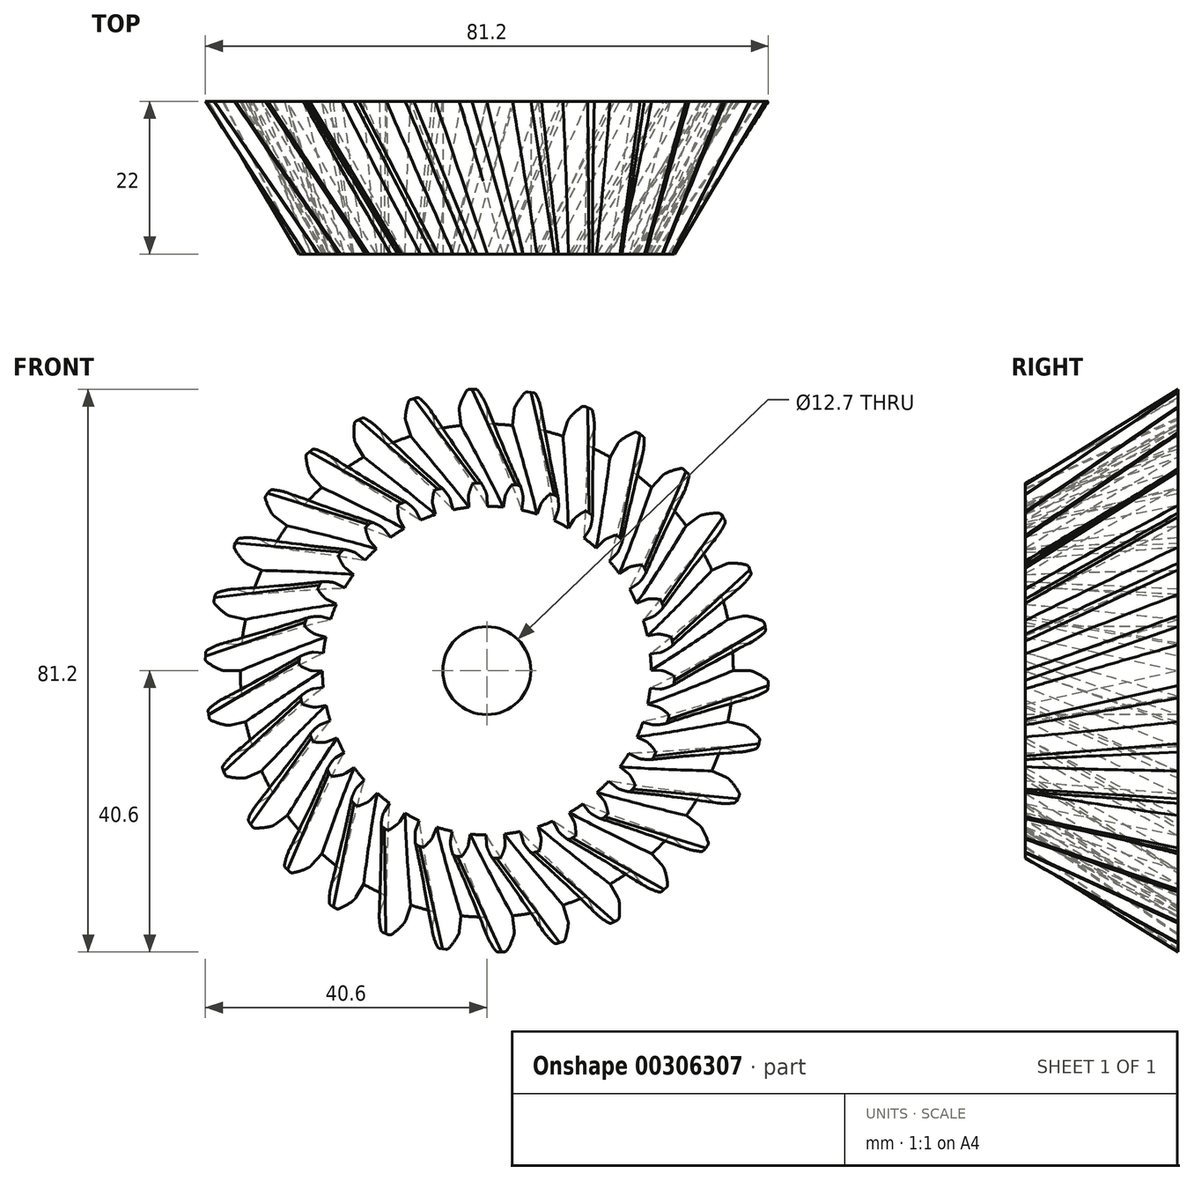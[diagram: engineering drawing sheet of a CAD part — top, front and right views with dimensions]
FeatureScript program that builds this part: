
annotation { "Feature Type Name" : "Feature", "Feature Type Description" : "" }
export const myFeature = defineFeature(function(context is Context, id is Id, definition is map)
    precondition{}
    {
        {
            var Q0;
            Q0=qCreatedBy(makeId("Front.planeOp"),FACE);
            var sketch = newSketch(context, id + "F0", { "sketchPlane" : qUnion([Q0])});
            skCircle(sketch, "E0", {"center": v(0, 0) * mm, "radius": 35.56 * mm});
            skArc(sketch, "E1", {"start": v(-0.13, 38.41) * mm, "mid": v(-0.64, 39.44) * mm, "end": v(-1.27, 40.4) * mm});
            skLineSegment(sketch, "E2", {"start": v(-1.7, 40.6) * mm, "end": v(-2.13, 40.58) * mm});
            skLineSegment(sketch, "E3", {"start": v(0, 37.8) * mm, "end": v(0, 35.56) * mm});
            skLineSegment(sketch, "E4.MirrorCS", {"start": v(-2.55, 40.56) * mm, "end": v(-2.13, 40.58) * mm});
            skArc(sketch, "E5.MirrorCS", {"start": v(-3.89, 38.22) * mm, "mid": v(-3.49, 39.3) * mm, "end": v(-2.96, 40.3) * mm});
            skLineSegment(sketch, "E6.MirrorCS", {"start": v(-3.95, 37.58) * mm, "end": v(-3.72, 35.37) * mm});
            skPoint(sketch, "E7.visualSharp", {"position": v(-1.44, 40.61) * mm});
            skArc(sketch, "E7.filletArc", {"start": v(-1.27, 40.4) * mm, "mid": v(-1.46, 40.55) * mm, "end": v(-1.7, 40.6) * mm});
            skPoint(sketch, "E8.visualSharp", {"position": v(-2.81, 40.54) * mm});
            skArc(sketch, "E8.filletArc", {"start": v(-2.55, 40.56) * mm, "mid": v(-2.78, 40.48) * mm, "end": v(-2.96, 40.3) * mm});
            skPoint(sketch, "E9.visualSharp", {"position": v(0, 38.1) * mm});
            skArc(sketch, "E9.filletArc", {"start": v(0, 37.8) * mm, "mid": v(-0.03, 38.1) * mm, "end": v(-0.13, 38.41) * mm});
            skPoint(sketch, "E10.visualSharp", {"position": v(-3.98, 37.9) * mm});
            skArc(sketch, "E10.filletArc", {"start": v(-3.89, 38.22) * mm, "mid": v(-3.95, 37.9) * mm, "end": v(-3.95, 37.58) * mm});
            skLineSegment(sketch, "E11.1.0", {"start": v(-11.68, 35.94) * mm, "end": v(-10.99, 33.82) * mm});
            skArc(sketch, "E11.1.1", {"start": v(-11.75, 36.57) * mm, "mid": v(-11.75, 36.25) * mm, "end": v(-11.68, 35.94) * mm});
            skArc(sketch, "E11.1.2", {"start": v(-11.75, 36.57) * mm, "mid": v(-11.58, 37.7) * mm, "end": v(-11.27, 38.81) * mm});
            skArc(sketch, "E11.1.3", {"start": v(-10.92, 39.14) * mm, "mid": v(-11.14, 39.02) * mm, "end": v(-11.27, 38.81) * mm});
            skLineSegment(sketch, "E11.1.4", {"start": v(-10.92, 39.14) * mm, "end": v(-10.52, 39.25) * mm});
            skLineSegment(sketch, "E11.1.5", {"start": v(-10.1, 39.36) * mm, "end": v(-10.52, 39.25) * mm});
            skArc(sketch, "E11.1.6", {"start": v(-9.64, 39.25) * mm, "mid": v(-9.86, 39.36) * mm, "end": v(-10.1, 39.36) * mm});
            skArc(sketch, "E11.1.7", {"start": v(-8.11, 37.55) * mm, "mid": v(-8.83, 38.45) * mm, "end": v(-9.64, 39.25) * mm});
            skArc(sketch, "E11.1.8", {"start": v(-7.86, 36.97) * mm, "mid": v(-7.95, 37.27) * mm, "end": v(-8.11, 37.55) * mm});
            skLineSegment(sketch, "E11.1.9", {"start": v(-7.86, 36.97) * mm, "end": v(-7.4, 34.78) * mm});
            skLineSegment(sketch, "E11.2.0", {"start": v(-18.9, 32.73) * mm, "end": v(-17.78, 30.8) * mm});
            skArc(sketch, "E11.2.1", {"start": v(-19.1, 33.33) * mm, "mid": v(-19.03, 33.02) * mm, "end": v(-18.9, 32.73) * mm});
            skArc(sketch, "E11.2.2", {"start": v(-19.1, 33.33) * mm, "mid": v(-19.17, 34.48) * mm, "end": v(-19.1, 35.62) * mm});
            skArc(sketch, "E11.2.3", {"start": v(-18.82, 36.01) * mm, "mid": v(-19, 35.85) * mm, "end": v(-19.1, 35.62) * mm});
            skLineSegment(sketch, "E11.2.4", {"start": v(-18.82, 36.01) * mm, "end": v(-18.45, 36.2) * mm});
            skLineSegment(sketch, "E11.2.5", {"start": v(-18.07, 36.4) * mm, "end": v(-18.45, 36.2) * mm});
            skArc(sketch, "E11.2.6", {"start": v(-17.6, 36.39) * mm, "mid": v(-17.83, 36.45) * mm, "end": v(-18.07, 36.4) * mm});
            skArc(sketch, "E11.2.7", {"start": v(-15.74, 35.04) * mm, "mid": v(-16.63, 35.77) * mm, "end": v(-17.6, 36.39) * mm});
            skArc(sketch, "E11.2.8", {"start": v(-15.37, 34.52) * mm, "mid": v(-15.53, 34.8) * mm, "end": v(-15.74, 35.04) * mm});
            skLineSegment(sketch, "E11.2.9", {"start": v(-15.37, 34.52) * mm, "end": v(-14.46, 32.49) * mm});
            skLineSegment(sketch, "E11.3.0", {"start": v(-25.29, 28.08) * mm, "end": v(-23.8, 26.43) * mm});
            skArc(sketch, "E11.3.1", {"start": v(-25.6, 28.63) * mm, "mid": v(-25.48, 28.34) * mm, "end": v(-25.29, 28.08) * mm});
            skArc(sketch, "E11.3.2", {"start": v(-25.6, 28.63) * mm, "mid": v(-25.92, 29.74) * mm, "end": v(-26.09, 30.87) * mm});
            skArc(sketch, "E11.3.3", {"start": v(-25.9, 31.31) * mm, "mid": v(-26.05, 31.12) * mm, "end": v(-26.09, 30.87) * mm});
            skLineSegment(sketch, "E11.3.4", {"start": v(-25.9, 31.31) * mm, "end": v(-25.57, 31.58) * mm});
            skLineSegment(sketch, "E11.3.5", {"start": v(-25.24, 31.84) * mm, "end": v(-25.57, 31.58) * mm});
            skArc(sketch, "E11.3.6", {"start": v(-24.77, 31.94) * mm, "mid": v(-25.02, 31.95) * mm, "end": v(-25.24, 31.84) * mm});
            skArc(sketch, "E11.3.7", {"start": v(-22.68, 31) * mm, "mid": v(-23.7, 31.53) * mm, "end": v(-24.77, 31.94) * mm});
            skArc(sketch, "E11.3.8", {"start": v(-22.21, 30.57) * mm, "mid": v(-22.43, 30.81) * mm, "end": v(-22.68, 31) * mm});
            skLineSegment(sketch, "E11.3.9", {"start": v(-22.21, 30.57) * mm, "end": v(-20.9, 28.77) * mm});
            skLineSegment(sketch, "E11.4.0", {"start": v(-30.57, 22.21) * mm, "end": v(-28.77, 20.9) * mm});
            skArc(sketch, "E11.4.1", {"start": v(-31, 22.68) * mm, "mid": v(-30.81, 22.43) * mm, "end": v(-30.57, 22.21) * mm});
            skArc(sketch, "E11.4.2", {"start": v(-31, 22.68) * mm, "mid": v(-31.53, 23.7) * mm, "end": v(-31.94, 24.77) * mm});
            skArc(sketch, "E11.4.3", {"start": v(-31.84, 25.24) * mm, "mid": v(-31.95, 25.02) * mm, "end": v(-31.94, 24.77) * mm});
            skLineSegment(sketch, "E11.4.4", {"start": v(-31.84, 25.24) * mm, "end": v(-31.58, 25.57) * mm});
            skLineSegment(sketch, "E11.4.5", {"start": v(-31.31, 25.9) * mm, "end": v(-31.58, 25.57) * mm});
            skArc(sketch, "E11.4.6", {"start": v(-30.87, 26.09) * mm, "mid": v(-31.12, 26.05) * mm, "end": v(-31.31, 25.9) * mm});
            skArc(sketch, "E11.4.7", {"start": v(-28.63, 25.6) * mm, "mid": v(-29.74, 25.92) * mm, "end": v(-30.87, 26.09) * mm});
            skArc(sketch, "E11.4.8", {"start": v(-28.08, 25.29) * mm, "mid": v(-28.34, 25.48) * mm, "end": v(-28.63, 25.6) * mm});
            skLineSegment(sketch, "E11.4.9", {"start": v(-28.08, 25.29) * mm, "end": v(-26.43, 23.8) * mm});
            skLineSegment(sketch, "E11.5.0", {"start": v(-34.52, 15.37) * mm, "end": v(-32.49, 14.46) * mm});
            skArc(sketch, "E11.5.1", {"start": v(-35.04, 15.74) * mm, "mid": v(-34.8, 15.53) * mm, "end": v(-34.52, 15.37) * mm});
            skArc(sketch, "E11.5.2", {"start": v(-35.04, 15.74) * mm, "mid": v(-35.77, 16.63) * mm, "end": v(-36.39, 17.6) * mm});
            skArc(sketch, "E11.5.3", {"start": v(-36.4, 18.07) * mm, "mid": v(-36.45, 17.83) * mm, "end": v(-36.39, 17.6) * mm});
            skLineSegment(sketch, "E11.5.4", {"start": v(-36.4, 18.07) * mm, "end": v(-36.2, 18.45) * mm});
            skLineSegment(sketch, "E11.5.5", {"start": v(-36.01, 18.82) * mm, "end": v(-36.2, 18.45) * mm});
            skArc(sketch, "E11.5.6", {"start": v(-35.62, 19.1) * mm, "mid": v(-35.85, 19) * mm, "end": v(-36.01, 18.82) * mm});
            skArc(sketch, "E11.5.7", {"start": v(-33.33, 19.1) * mm, "mid": v(-34.48, 19.17) * mm, "end": v(-35.62, 19.1) * mm});
            skArc(sketch, "E11.5.8", {"start": v(-32.73, 18.9) * mm, "mid": v(-33.02, 19.03) * mm, "end": v(-33.33, 19.1) * mm});
            skLineSegment(sketch, "E11.5.9", {"start": v(-32.73, 18.9) * mm, "end": v(-30.8, 17.78) * mm});
            skLineSegment(sketch, "E11.6.0", {"start": v(-36.97, 7.86) * mm, "end": v(-34.78, 7.4) * mm});
            skArc(sketch, "E11.6.1", {"start": v(-37.55, 8.11) * mm, "mid": v(-37.27, 7.95) * mm, "end": v(-36.97, 7.86) * mm});
            skArc(sketch, "E11.6.2", {"start": v(-37.55, 8.11) * mm, "mid": v(-38.45, 8.83) * mm, "end": v(-39.25, 9.64) * mm});
            skArc(sketch, "E11.6.3", {"start": v(-39.36, 10.1) * mm, "mid": v(-39.36, 9.86) * mm, "end": v(-39.25, 9.64) * mm});
            skLineSegment(sketch, "E11.6.4", {"start": v(-39.36, 10.1) * mm, "end": v(-39.25, 10.52) * mm});
            skLineSegment(sketch, "E11.6.5", {"start": v(-39.14, 10.92) * mm, "end": v(-39.25, 10.52) * mm});
            skArc(sketch, "E11.6.6", {"start": v(-38.81, 11.27) * mm, "mid": v(-39.02, 11.14) * mm, "end": v(-39.14, 10.92) * mm});
            skArc(sketch, "E11.6.7", {"start": v(-36.57, 11.75) * mm, "mid": v(-37.7, 11.58) * mm, "end": v(-38.81, 11.27) * mm});
            skArc(sketch, "E11.6.8", {"start": v(-35.94, 11.68) * mm, "mid": v(-36.25, 11.75) * mm, "end": v(-36.57, 11.75) * mm});
            skLineSegment(sketch, "E11.6.9", {"start": v(-35.94, 11.68) * mm, "end": v(-33.82, 10.99) * mm});
            skLineSegment(sketch, "E11.7.0", {"start": v(-37.8, 0) * mm, "end": v(-35.56, 0) * mm});
            skArc(sketch, "E11.7.1", {"start": v(-38.41, 0.13) * mm, "mid": v(-38.1, 0.03) * mm, "end": v(-37.8, 0) * mm});
            skArc(sketch, "E11.7.2", {"start": v(-38.41, 0.13) * mm, "mid": v(-39.44, 0.64) * mm, "end": v(-40.4, 1.27) * mm});
            skArc(sketch, "E11.7.3", {"start": v(-40.6, 1.7) * mm, "mid": v(-40.55, 1.46) * mm, "end": v(-40.4, 1.27) * mm});
            skLineSegment(sketch, "E11.7.4", {"start": v(-40.6, 1.7) * mm, "end": v(-40.58, 2.13) * mm});
            skLineSegment(sketch, "E11.7.5", {"start": v(-40.56, 2.55) * mm, "end": v(-40.58, 2.13) * mm});
            skArc(sketch, "E11.7.6", {"start": v(-40.3, 2.96) * mm, "mid": v(-40.48, 2.78) * mm, "end": v(-40.56, 2.55) * mm});
            skArc(sketch, "E11.7.7", {"start": v(-38.22, 3.89) * mm, "mid": v(-39.3, 3.49) * mm, "end": v(-40.3, 2.96) * mm});
            skArc(sketch, "E11.7.8", {"start": v(-37.58, 3.95) * mm, "mid": v(-37.9, 3.95) * mm, "end": v(-38.22, 3.89) * mm});
            skLineSegment(sketch, "E11.7.9", {"start": v(-37.58, 3.95) * mm, "end": v(-35.37, 3.72) * mm});
            skLineSegment(sketch, "E11.8.0", {"start": v(-36.97, -7.86) * mm, "end": v(-34.78, -7.4) * mm});
            skArc(sketch, "E11.8.1", {"start": v(-37.6, -7.86) * mm, "mid": v(-37.28, -7.9) * mm, "end": v(-36.97, -7.86) * mm});
            skArc(sketch, "E11.8.2", {"start": v(-37.6, -7.86) * mm, "mid": v(-38.71, -7.57) * mm, "end": v(-39.78, -7.16) * mm});
            skArc(sketch, "E11.8.3", {"start": v(-40.07, -6.77) * mm, "mid": v(-39.97, -7) * mm, "end": v(-39.78, -7.16) * mm});
            skLineSegment(sketch, "E11.8.4", {"start": v(-40.07, -6.77) * mm, "end": v(-40.13, -6.36) * mm});
            skLineSegment(sketch, "E11.8.5", {"start": v(-40.2, -5.94) * mm, "end": v(-40.13, -6.36) * mm});
            skArc(sketch, "E11.8.6", {"start": v(-40.04, -5.49) * mm, "mid": v(-40.18, -5.7) * mm, "end": v(-40.2, -5.94) * mm});
            skArc(sketch, "E11.8.7", {"start": v(-38.19, -4.14) * mm, "mid": v(-39.16, -4.76) * mm, "end": v(-40.04, -5.49) * mm});
            skArc(sketch, "E11.8.8", {"start": v(-37.58, -3.95) * mm, "mid": v(-37.9, -4.02) * mm, "end": v(-38.19, -4.14) * mm});
            skLineSegment(sketch, "E11.8.9", {"start": v(-37.58, -3.95) * mm, "end": v(-35.37, -3.72) * mm});
            skLineSegment(sketch, "E11.9.0", {"start": v(-34.52, -15.37) * mm, "end": v(-32.49, -14.46) * mm});
            skArc(sketch, "E11.9.1", {"start": v(-35.14, -15.5) * mm, "mid": v(-34.83, -15.47) * mm, "end": v(-34.52, -15.37) * mm});
            skArc(sketch, "E11.9.2", {"start": v(-35.14, -15.5) * mm, "mid": v(-36.3, -15.46) * mm, "end": v(-37.42, -15.27) * mm});
            skArc(sketch, "E11.9.3", {"start": v(-37.78, -14.96) * mm, "mid": v(-37.64, -15.16) * mm, "end": v(-37.42, -15.27) * mm});
            skLineSegment(sketch, "E11.9.4", {"start": v(-37.78, -14.96) * mm, "end": v(-37.94, -14.56) * mm});
            skLineSegment(sketch, "E11.9.5", {"start": v(-38.09, -14.17) * mm, "end": v(-37.94, -14.56) * mm});
            skArc(sketch, "E11.9.6", {"start": v(-38.03, -13.7) * mm, "mid": v(-38.12, -13.92) * mm, "end": v(-38.09, -14.17) * mm});
            skArc(sketch, "E11.9.7", {"start": v(-36.5, -12) * mm, "mid": v(-37.31, -12.8) * mm, "end": v(-38.03, -13.7) * mm});
            skArc(sketch, "E11.9.8", {"start": v(-35.94, -11.68) * mm, "mid": v(-36.23, -11.8) * mm, "end": v(-36.5, -12) * mm});
            skLineSegment(sketch, "E11.9.9", {"start": v(-35.94, -11.68) * mm, "end": v(-33.82, -10.99) * mm});
            skLineSegment(sketch, "E11.10.0", {"start": v(-30.57, -22.21) * mm, "end": v(-28.77, -20.9) * mm});
            skArc(sketch, "E11.10.1", {"start": v(-31.15, -22.48) * mm, "mid": v(-30.85, -22.37) * mm, "end": v(-30.57, -22.21) * mm});
            skArc(sketch, "E11.10.2", {"start": v(-31.15, -22.48) * mm, "mid": v(-32.28, -22.67) * mm, "end": v(-33.43, -22.72) * mm});
            skArc(sketch, "E11.10.3", {"start": v(-33.85, -22.49) * mm, "mid": v(-33.67, -22.65) * mm, "end": v(-33.43, -22.72) * mm});
            skLineSegment(sketch, "E11.10.4", {"start": v(-33.85, -22.49) * mm, "end": v(-34.08, -22.13) * mm});
            skLineSegment(sketch, "E11.10.5", {"start": v(-34.3, -21.78) * mm, "end": v(-34.08, -22.13) * mm});
            skArc(sketch, "E11.10.6", {"start": v(-34.35, -21.3) * mm, "mid": v(-34.39, -21.54) * mm, "end": v(-34.3, -21.78) * mm});
            skArc(sketch, "E11.10.7", {"start": v(-33.2, -19.32) * mm, "mid": v(-33.84, -20.27) * mm, "end": v(-34.35, -21.3) * mm});
            skArc(sketch, "E11.10.8", {"start": v(-32.73, -18.9) * mm, "mid": v(-32.99, -19.08) * mm, "end": v(-33.2, -19.32) * mm});
            skLineSegment(sketch, "E11.10.9", {"start": v(-32.73, -18.9) * mm, "end": v(-30.8, -17.78) * mm});
            skLineSegment(sketch, "E11.11.0", {"start": v(-25.29, -28.08) * mm, "end": v(-23.8, -26.43) * mm});
            skArc(sketch, "E11.11.1", {"start": v(-25.8, -28.46) * mm, "mid": v(-25.52, -28.3) * mm, "end": v(-25.29, -28.08) * mm});
            skArc(sketch, "E11.11.2", {"start": v(-25.8, -28.46) * mm, "mid": v(-26.87, -28.88) * mm, "end": v(-27.98, -29.17) * mm});
            skArc(sketch, "E11.11.3", {"start": v(-28.43, -29.03) * mm, "mid": v(-28.22, -29.16) * mm, "end": v(-27.98, -29.17) * mm});
            skLineSegment(sketch, "E11.11.4", {"start": v(-28.43, -29.03) * mm, "end": v(-28.73, -28.73) * mm});
            skLineSegment(sketch, "E11.11.5", {"start": v(-29.03, -28.43) * mm, "end": v(-28.73, -28.73) * mm});
            skArc(sketch, "E11.11.6", {"start": v(-29.17, -27.98) * mm, "mid": v(-29.16, -28.22) * mm, "end": v(-29.03, -28.43) * mm});
            skArc(sketch, "E11.11.7", {"start": v(-28.46, -25.8) * mm, "mid": v(-28.88, -26.87) * mm, "end": v(-29.17, -27.98) * mm});
            skArc(sketch, "E11.11.8", {"start": v(-28.08, -25.29) * mm, "mid": v(-28.3, -25.52) * mm, "end": v(-28.46, -25.8) * mm});
            skLineSegment(sketch, "E11.11.9", {"start": v(-28.08, -25.29) * mm, "end": v(-26.43, -23.8) * mm});
            skLineSegment(sketch, "E11.12.0", {"start": v(-18.9, -32.73) * mm, "end": v(-17.78, -30.8) * mm});
            skArc(sketch, "E11.12.1", {"start": v(-19.32, -33.2) * mm, "mid": v(-19.08, -32.99) * mm, "end": v(-18.9, -32.73) * mm});
            skArc(sketch, "E11.12.2", {"start": v(-19.32, -33.2) * mm, "mid": v(-20.27, -33.84) * mm, "end": v(-21.3, -34.35) * mm});
            skArc(sketch, "E11.12.3", {"start": v(-21.78, -34.3) * mm, "mid": v(-21.54, -34.39) * mm, "end": v(-21.3, -34.35) * mm});
            skLineSegment(sketch, "E11.12.4", {"start": v(-21.78, -34.3) * mm, "end": v(-22.13, -34.08) * mm});
            skLineSegment(sketch, "E11.12.5", {"start": v(-22.49, -33.85) * mm, "end": v(-22.13, -34.08) * mm});
            skArc(sketch, "E11.12.6", {"start": v(-22.72, -33.43) * mm, "mid": v(-22.65, -33.67) * mm, "end": v(-22.49, -33.85) * mm});
            skArc(sketch, "E11.12.7", {"start": v(-22.48, -31.15) * mm, "mid": v(-22.67, -32.28) * mm, "end": v(-22.72, -33.43) * mm});
            skArc(sketch, "E11.12.8", {"start": v(-22.21, -30.57) * mm, "mid": v(-22.37, -30.85) * mm, "end": v(-22.48, -31.15) * mm});
            skLineSegment(sketch, "E11.12.9", {"start": v(-22.21, -30.57) * mm, "end": v(-20.9, -28.77) * mm});
            skLineSegment(sketch, "E11.13.0", {"start": v(-11.68, -35.94) * mm, "end": v(-10.99, -33.82) * mm});
            skArc(sketch, "E11.13.1", {"start": v(-12, -36.5) * mm, "mid": v(-11.8, -36.23) * mm, "end": v(-11.68, -35.94) * mm});
            skArc(sketch, "E11.13.2", {"start": v(-12, -36.5) * mm, "mid": v(-12.8, -37.31) * mm, "end": v(-13.7, -38.03) * mm});
            skArc(sketch, "E11.13.3", {"start": v(-14.17, -38.09) * mm, "mid": v(-13.92, -38.12) * mm, "end": v(-13.7, -38.03) * mm});
            skLineSegment(sketch, "E11.13.4", {"start": v(-14.17, -38.09) * mm, "end": v(-14.56, -37.94) * mm});
            skLineSegment(sketch, "E11.13.5", {"start": v(-14.96, -37.78) * mm, "end": v(-14.56, -37.94) * mm});
            skArc(sketch, "E11.13.6", {"start": v(-15.27, -37.42) * mm, "mid": v(-15.16, -37.64) * mm, "end": v(-14.96, -37.78) * mm});
            skArc(sketch, "E11.13.7", {"start": v(-15.5, -35.14) * mm, "mid": v(-15.46, -36.3) * mm, "end": v(-15.27, -37.42) * mm});
            skArc(sketch, "E11.13.8", {"start": v(-15.37, -34.52) * mm, "mid": v(-15.47, -34.83) * mm, "end": v(-15.5, -35.14) * mm});
            skLineSegment(sketch, "E11.13.9", {"start": v(-15.37, -34.52) * mm, "end": v(-14.46, -32.49) * mm});
            skLineSegment(sketch, "E11.14.0", {"start": v(-3.95, -37.58) * mm, "end": v(-3.72, -35.37) * mm});
            skArc(sketch, "E11.14.1", {"start": v(-4.14, -38.19) * mm, "mid": v(-4.02, -37.9) * mm, "end": v(-3.95, -37.58) * mm});
            skArc(sketch, "E11.14.2", {"start": v(-4.14, -38.19) * mm, "mid": v(-4.76, -39.16) * mm, "end": v(-5.49, -40.04) * mm});
            skArc(sketch, "E11.14.3", {"start": v(-5.94, -40.2) * mm, "mid": v(-5.7, -40.18) * mm, "end": v(-5.49, -40.04) * mm});
            skLineSegment(sketch, "E11.14.4", {"start": v(-5.94, -40.2) * mm, "end": v(-6.36, -40.13) * mm});
            skLineSegment(sketch, "E11.14.5", {"start": v(-6.77, -40.07) * mm, "end": v(-6.36, -40.13) * mm});
            skArc(sketch, "E11.14.6", {"start": v(-7.16, -39.78) * mm, "mid": v(-7, -39.97) * mm, "end": v(-6.77, -40.07) * mm});
            skArc(sketch, "E11.14.7", {"start": v(-7.86, -37.6) * mm, "mid": v(-7.57, -38.71) * mm, "end": v(-7.16, -39.78) * mm});
            skArc(sketch, "E11.14.8", {"start": v(-7.86, -36.97) * mm, "mid": v(-7.9, -37.28) * mm, "end": v(-7.86, -37.6) * mm});
            skLineSegment(sketch, "E11.14.9", {"start": v(-7.86, -36.97) * mm, "end": v(-7.4, -34.78) * mm});
            skLineSegment(sketch, "E11.15.0", {"start": v(3.95, -37.58) * mm, "end": v(3.72, -35.37) * mm});
            skArc(sketch, "E11.15.1", {"start": v(3.89, -38.22) * mm, "mid": v(3.95, -37.9) * mm, "end": v(3.95, -37.58) * mm});
            skArc(sketch, "E11.15.2", {"start": v(3.89, -38.22) * mm, "mid": v(3.49, -39.3) * mm, "end": v(2.96, -40.3) * mm});
            skArc(sketch, "E11.15.3", {"start": v(2.55, -40.56) * mm, "mid": v(2.78, -40.48) * mm, "end": v(2.96, -40.3) * mm});
            skLineSegment(sketch, "E11.15.4", {"start": v(2.55, -40.56) * mm, "end": v(2.13, -40.58) * mm});
            skLineSegment(sketch, "E11.15.5", {"start": v(1.7, -40.6) * mm, "end": v(2.13, -40.58) * mm});
            skArc(sketch, "E11.15.6", {"start": v(1.27, -40.4) * mm, "mid": v(1.46, -40.55) * mm, "end": v(1.7, -40.6) * mm});
            skArc(sketch, "E11.15.7", {"start": v(0.13, -38.41) * mm, "mid": v(0.64, -39.44) * mm, "end": v(1.27, -40.4) * mm});
            skArc(sketch, "E11.15.8", {"start": v(0, -37.8) * mm, "mid": v(0.03, -38.1) * mm, "end": v(0.13, -38.41) * mm});
            skLineSegment(sketch, "E11.15.9", {"start": v(0, -37.8) * mm, "end": v(0, -35.56) * mm});
            skLineSegment(sketch, "E11.16.0", {"start": v(11.68, -35.94) * mm, "end": v(10.99, -33.82) * mm});
            skArc(sketch, "E11.16.1", {"start": v(11.75, -36.57) * mm, "mid": v(11.75, -36.25) * mm, "end": v(11.68, -35.94) * mm});
            skArc(sketch, "E11.16.2", {"start": v(11.75, -36.57) * mm, "mid": v(11.58, -37.7) * mm, "end": v(11.27, -38.81) * mm});
            skArc(sketch, "E11.16.3", {"start": v(10.92, -39.14) * mm, "mid": v(11.14, -39.02) * mm, "end": v(11.27, -38.81) * mm});
            skLineSegment(sketch, "E11.16.4", {"start": v(10.92, -39.14) * mm, "end": v(10.52, -39.25) * mm});
            skLineSegment(sketch, "E11.16.5", {"start": v(10.1, -39.36) * mm, "end": v(10.52, -39.25) * mm});
            skArc(sketch, "E11.16.6", {"start": v(9.64, -39.25) * mm, "mid": v(9.86, -39.36) * mm, "end": v(10.1, -39.36) * mm});
            skArc(sketch, "E11.16.7", {"start": v(8.11, -37.55) * mm, "mid": v(8.83, -38.45) * mm, "end": v(9.64, -39.25) * mm});
            skArc(sketch, "E11.16.8", {"start": v(7.86, -36.97) * mm, "mid": v(7.95, -37.27) * mm, "end": v(8.11, -37.55) * mm});
            skLineSegment(sketch, "E11.16.9", {"start": v(7.86, -36.97) * mm, "end": v(7.4, -34.78) * mm});
            skLineSegment(sketch, "E11.17.0", {"start": v(18.9, -32.73) * mm, "end": v(17.78, -30.8) * mm});
            skArc(sketch, "E11.17.1", {"start": v(19.1, -33.33) * mm, "mid": v(19.03, -33.02) * mm, "end": v(18.9, -32.73) * mm});
            skArc(sketch, "E11.17.2", {"start": v(19.1, -33.33) * mm, "mid": v(19.17, -34.48) * mm, "end": v(19.1, -35.62) * mm});
            skArc(sketch, "E11.17.3", {"start": v(18.82, -36.01) * mm, "mid": v(19, -35.85) * mm, "end": v(19.1, -35.62) * mm});
            skLineSegment(sketch, "E11.17.4", {"start": v(18.82, -36.01) * mm, "end": v(18.45, -36.2) * mm});
            skLineSegment(sketch, "E11.17.5", {"start": v(18.07, -36.4) * mm, "end": v(18.45, -36.2) * mm});
            skArc(sketch, "E11.17.6", {"start": v(17.6, -36.39) * mm, "mid": v(17.83, -36.45) * mm, "end": v(18.07, -36.4) * mm});
            skArc(sketch, "E11.17.7", {"start": v(15.74, -35.04) * mm, "mid": v(16.63, -35.77) * mm, "end": v(17.6, -36.39) * mm});
            skArc(sketch, "E11.17.8", {"start": v(15.37, -34.52) * mm, "mid": v(15.53, -34.8) * mm, "end": v(15.74, -35.04) * mm});
            skLineSegment(sketch, "E11.17.9", {"start": v(15.37, -34.52) * mm, "end": v(14.46, -32.49) * mm});
            skLineSegment(sketch, "E11.18.0", {"start": v(25.29, -28.08) * mm, "end": v(23.8, -26.43) * mm});
            skArc(sketch, "E11.18.1", {"start": v(25.6, -28.63) * mm, "mid": v(25.48, -28.34) * mm, "end": v(25.29, -28.08) * mm});
            skArc(sketch, "E11.18.2", {"start": v(25.6, -28.63) * mm, "mid": v(25.92, -29.74) * mm, "end": v(26.09, -30.87) * mm});
            skArc(sketch, "E11.18.3", {"start": v(25.9, -31.31) * mm, "mid": v(26.05, -31.12) * mm, "end": v(26.09, -30.87) * mm});
            skLineSegment(sketch, "E11.18.4", {"start": v(25.9, -31.31) * mm, "end": v(25.57, -31.58) * mm});
            skLineSegment(sketch, "E11.18.5", {"start": v(25.24, -31.84) * mm, "end": v(25.57, -31.58) * mm});
            skArc(sketch, "E11.18.6", {"start": v(24.77, -31.94) * mm, "mid": v(25.02, -31.95) * mm, "end": v(25.24, -31.84) * mm});
            skArc(sketch, "E11.18.7", {"start": v(22.68, -31) * mm, "mid": v(23.7, -31.53) * mm, "end": v(24.77, -31.94) * mm});
            skArc(sketch, "E11.18.8", {"start": v(22.21, -30.57) * mm, "mid": v(22.43, -30.81) * mm, "end": v(22.68, -31) * mm});
            skLineSegment(sketch, "E11.18.9", {"start": v(22.21, -30.57) * mm, "end": v(20.9, -28.77) * mm});
            skLineSegment(sketch, "E11.19.0", {"start": v(30.57, -22.21) * mm, "end": v(28.77, -20.9) * mm});
            skArc(sketch, "E11.19.1", {"start": v(31, -22.68) * mm, "mid": v(30.81, -22.43) * mm, "end": v(30.57, -22.21) * mm});
            skArc(sketch, "E11.19.2", {"start": v(31, -22.68) * mm, "mid": v(31.53, -23.7) * mm, "end": v(31.94, -24.77) * mm});
            skArc(sketch, "E11.19.3", {"start": v(31.84, -25.24) * mm, "mid": v(31.95, -25.02) * mm, "end": v(31.94, -24.77) * mm});
            skLineSegment(sketch, "E11.19.4", {"start": v(31.84, -25.24) * mm, "end": v(31.58, -25.57) * mm});
            skLineSegment(sketch, "E11.19.5", {"start": v(31.31, -25.9) * mm, "end": v(31.58, -25.57) * mm});
            skArc(sketch, "E11.19.6", {"start": v(30.87, -26.09) * mm, "mid": v(31.12, -26.05) * mm, "end": v(31.31, -25.9) * mm});
            skArc(sketch, "E11.19.7", {"start": v(28.63, -25.6) * mm, "mid": v(29.74, -25.92) * mm, "end": v(30.87, -26.09) * mm});
            skArc(sketch, "E11.19.8", {"start": v(28.08, -25.29) * mm, "mid": v(28.34, -25.48) * mm, "end": v(28.63, -25.6) * mm});
            skLineSegment(sketch, "E11.19.9", {"start": v(28.08, -25.29) * mm, "end": v(26.43, -23.8) * mm});
            skLineSegment(sketch, "E11.20.0", {"start": v(34.52, -15.37) * mm, "end": v(32.49, -14.46) * mm});
            skArc(sketch, "E11.20.1", {"start": v(35.04, -15.74) * mm, "mid": v(34.8, -15.53) * mm, "end": v(34.52, -15.37) * mm});
            skArc(sketch, "E11.20.2", {"start": v(35.04, -15.74) * mm, "mid": v(35.77, -16.63) * mm, "end": v(36.39, -17.6) * mm});
            skArc(sketch, "E11.20.3", {"start": v(36.4, -18.07) * mm, "mid": v(36.45, -17.83) * mm, "end": v(36.39, -17.6) * mm});
            skLineSegment(sketch, "E11.20.4", {"start": v(36.4, -18.07) * mm, "end": v(36.2, -18.45) * mm});
            skLineSegment(sketch, "E11.20.5", {"start": v(36.01, -18.82) * mm, "end": v(36.2, -18.45) * mm});
            skArc(sketch, "E11.20.6", {"start": v(35.62, -19.1) * mm, "mid": v(35.85, -19) * mm, "end": v(36.01, -18.82) * mm});
            skArc(sketch, "E11.20.7", {"start": v(33.33, -19.1) * mm, "mid": v(34.48, -19.17) * mm, "end": v(35.62, -19.1) * mm});
            skArc(sketch, "E11.20.8", {"start": v(32.73, -18.9) * mm, "mid": v(33.02, -19.03) * mm, "end": v(33.33, -19.1) * mm});
            skLineSegment(sketch, "E11.20.9", {"start": v(32.73, -18.9) * mm, "end": v(30.8, -17.78) * mm});
            skLineSegment(sketch, "E11.21.0", {"start": v(36.97, -7.86) * mm, "end": v(34.78, -7.4) * mm});
            skArc(sketch, "E11.21.1", {"start": v(37.55, -8.11) * mm, "mid": v(37.27, -7.95) * mm, "end": v(36.97, -7.86) * mm});
            skArc(sketch, "E11.21.2", {"start": v(37.55, -8.11) * mm, "mid": v(38.45, -8.83) * mm, "end": v(39.25, -9.64) * mm});
            skArc(sketch, "E11.21.3", {"start": v(39.36, -10.1) * mm, "mid": v(39.36, -9.86) * mm, "end": v(39.25, -9.64) * mm});
            skLineSegment(sketch, "E11.21.4", {"start": v(39.36, -10.1) * mm, "end": v(39.25, -10.52) * mm});
            skLineSegment(sketch, "E11.21.5", {"start": v(39.14, -10.92) * mm, "end": v(39.25, -10.52) * mm});
            skArc(sketch, "E11.21.6", {"start": v(38.81, -11.27) * mm, "mid": v(39.02, -11.14) * mm, "end": v(39.14, -10.92) * mm});
            skArc(sketch, "E11.21.7", {"start": v(36.57, -11.75) * mm, "mid": v(37.7, -11.58) * mm, "end": v(38.81, -11.27) * mm});
            skArc(sketch, "E11.21.8", {"start": v(35.94, -11.68) * mm, "mid": v(36.25, -11.75) * mm, "end": v(36.57, -11.75) * mm});
            skLineSegment(sketch, "E11.21.9", {"start": v(35.94, -11.68) * mm, "end": v(33.82, -10.99) * mm});
            skLineSegment(sketch, "E11.22.0", {"start": v(37.8, 0) * mm, "end": v(35.56, 0) * mm});
            skArc(sketch, "E11.22.1", {"start": v(38.41, -0.13) * mm, "mid": v(38.1, -0.03) * mm, "end": v(37.8, 0) * mm});
            skArc(sketch, "E11.22.2", {"start": v(38.41, -0.13) * mm, "mid": v(39.44, -0.64) * mm, "end": v(40.4, -1.27) * mm});
            skArc(sketch, "E11.22.3", {"start": v(40.6, -1.7) * mm, "mid": v(40.55, -1.46) * mm, "end": v(40.4, -1.27) * mm});
            skLineSegment(sketch, "E11.22.4", {"start": v(40.6, -1.7) * mm, "end": v(40.58, -2.13) * mm});
            skLineSegment(sketch, "E11.22.5", {"start": v(40.56, -2.55) * mm, "end": v(40.58, -2.13) * mm});
            skArc(sketch, "E11.22.6", {"start": v(40.3, -2.96) * mm, "mid": v(40.48, -2.78) * mm, "end": v(40.56, -2.55) * mm});
            skArc(sketch, "E11.22.7", {"start": v(38.22, -3.89) * mm, "mid": v(39.3, -3.49) * mm, "end": v(40.3, -2.96) * mm});
            skArc(sketch, "E11.22.8", {"start": v(37.58, -3.95) * mm, "mid": v(37.9, -3.95) * mm, "end": v(38.22, -3.89) * mm});
            skLineSegment(sketch, "E11.22.9", {"start": v(37.58, -3.95) * mm, "end": v(35.37, -3.72) * mm});
            skLineSegment(sketch, "E11.23.0", {"start": v(36.97, 7.86) * mm, "end": v(34.78, 7.4) * mm});
            skArc(sketch, "E11.23.1", {"start": v(37.6, 7.86) * mm, "mid": v(37.28, 7.9) * mm, "end": v(36.97, 7.86) * mm});
            skArc(sketch, "E11.23.2", {"start": v(37.6, 7.86) * mm, "mid": v(38.71, 7.57) * mm, "end": v(39.78, 7.16) * mm});
            skArc(sketch, "E11.23.3", {"start": v(40.07, 6.77) * mm, "mid": v(39.97, 7) * mm, "end": v(39.78, 7.16) * mm});
            skLineSegment(sketch, "E11.23.4", {"start": v(40.07, 6.77) * mm, "end": v(40.13, 6.36) * mm});
            skLineSegment(sketch, "E11.23.5", {"start": v(40.2, 5.94) * mm, "end": v(40.13, 6.36) * mm});
            skArc(sketch, "E11.23.6", {"start": v(40.04, 5.49) * mm, "mid": v(40.18, 5.7) * mm, "end": v(40.2, 5.94) * mm});
            skArc(sketch, "E11.23.7", {"start": v(38.19, 4.14) * mm, "mid": v(39.16, 4.76) * mm, "end": v(40.04, 5.49) * mm});
            skArc(sketch, "E11.23.8", {"start": v(37.58, 3.95) * mm, "mid": v(37.9, 4.02) * mm, "end": v(38.19, 4.14) * mm});
            skLineSegment(sketch, "E11.23.9", {"start": v(37.58, 3.95) * mm, "end": v(35.37, 3.72) * mm});
            skLineSegment(sketch, "E11.24.0", {"start": v(34.52, 15.37) * mm, "end": v(32.49, 14.46) * mm});
            skArc(sketch, "E11.24.1", {"start": v(35.14, 15.5) * mm, "mid": v(34.83, 15.47) * mm, "end": v(34.52, 15.37) * mm});
            skArc(sketch, "E11.24.2", {"start": v(35.14, 15.5) * mm, "mid": v(36.3, 15.46) * mm, "end": v(37.42, 15.27) * mm});
            skArc(sketch, "E11.24.3", {"start": v(37.78, 14.96) * mm, "mid": v(37.64, 15.16) * mm, "end": v(37.42, 15.27) * mm});
            skLineSegment(sketch, "E11.24.4", {"start": v(37.78, 14.96) * mm, "end": v(37.94, 14.56) * mm});
            skLineSegment(sketch, "E11.24.5", {"start": v(38.09, 14.17) * mm, "end": v(37.94, 14.56) * mm});
            skArc(sketch, "E11.24.6", {"start": v(38.03, 13.7) * mm, "mid": v(38.12, 13.92) * mm, "end": v(38.09, 14.17) * mm});
            skArc(sketch, "E11.24.7", {"start": v(36.5, 12) * mm, "mid": v(37.31, 12.8) * mm, "end": v(38.03, 13.7) * mm});
            skArc(sketch, "E11.24.8", {"start": v(35.94, 11.68) * mm, "mid": v(36.23, 11.8) * mm, "end": v(36.5, 12) * mm});
            skLineSegment(sketch, "E11.24.9", {"start": v(35.94, 11.68) * mm, "end": v(33.82, 10.99) * mm});
            skLineSegment(sketch, "E11.25.0", {"start": v(30.57, 22.21) * mm, "end": v(28.77, 20.9) * mm});
            skArc(sketch, "E11.25.1", {"start": v(31.15, 22.48) * mm, "mid": v(30.85, 22.37) * mm, "end": v(30.57, 22.21) * mm});
            skArc(sketch, "E11.25.2", {"start": v(31.15, 22.48) * mm, "mid": v(32.28, 22.67) * mm, "end": v(33.43, 22.72) * mm});
            skArc(sketch, "E11.25.3", {"start": v(33.85, 22.49) * mm, "mid": v(33.67, 22.65) * mm, "end": v(33.43, 22.72) * mm});
            skLineSegment(sketch, "E11.25.4", {"start": v(33.85, 22.49) * mm, "end": v(34.08, 22.13) * mm});
            skLineSegment(sketch, "E11.25.5", {"start": v(34.3, 21.78) * mm, "end": v(34.08, 22.13) * mm});
            skArc(sketch, "E11.25.6", {"start": v(34.35, 21.3) * mm, "mid": v(34.39, 21.54) * mm, "end": v(34.3, 21.78) * mm});
            skArc(sketch, "E11.25.7", {"start": v(33.2, 19.32) * mm, "mid": v(33.84, 20.27) * mm, "end": v(34.35, 21.3) * mm});
            skArc(sketch, "E11.25.8", {"start": v(32.73, 18.9) * mm, "mid": v(32.99, 19.08) * mm, "end": v(33.2, 19.32) * mm});
            skLineSegment(sketch, "E11.25.9", {"start": v(32.73, 18.9) * mm, "end": v(30.8, 17.78) * mm});
            skLineSegment(sketch, "E11.26.0", {"start": v(25.29, 28.08) * mm, "end": v(23.8, 26.43) * mm});
            skArc(sketch, "E11.26.1", {"start": v(25.8, 28.46) * mm, "mid": v(25.52, 28.3) * mm, "end": v(25.29, 28.08) * mm});
            skArc(sketch, "E11.26.2", {"start": v(25.8, 28.46) * mm, "mid": v(26.87, 28.88) * mm, "end": v(27.98, 29.17) * mm});
            skArc(sketch, "E11.26.3", {"start": v(28.43, 29.03) * mm, "mid": v(28.22, 29.16) * mm, "end": v(27.98, 29.17) * mm});
            skLineSegment(sketch, "E11.26.4", {"start": v(28.43, 29.03) * mm, "end": v(28.73, 28.73) * mm});
            skLineSegment(sketch, "E11.26.5", {"start": v(29.03, 28.43) * mm, "end": v(28.73, 28.73) * mm});
            skArc(sketch, "E11.26.6", {"start": v(29.17, 27.98) * mm, "mid": v(29.16, 28.22) * mm, "end": v(29.03, 28.43) * mm});
            skArc(sketch, "E11.26.7", {"start": v(28.46, 25.8) * mm, "mid": v(28.88, 26.87) * mm, "end": v(29.17, 27.98) * mm});
            skArc(sketch, "E11.26.8", {"start": v(28.08, 25.29) * mm, "mid": v(28.3, 25.52) * mm, "end": v(28.46, 25.8) * mm});
            skLineSegment(sketch, "E11.26.9", {"start": v(28.08, 25.29) * mm, "end": v(26.43, 23.8) * mm});
            skLineSegment(sketch, "E11.27.0", {"start": v(18.9, 32.73) * mm, "end": v(17.78, 30.8) * mm});
            skArc(sketch, "E11.27.1", {"start": v(19.32, 33.2) * mm, "mid": v(19.08, 32.99) * mm, "end": v(18.9, 32.73) * mm});
            skArc(sketch, "E11.27.2", {"start": v(19.32, 33.2) * mm, "mid": v(20.27, 33.84) * mm, "end": v(21.3, 34.35) * mm});
            skArc(sketch, "E11.27.3", {"start": v(21.78, 34.3) * mm, "mid": v(21.54, 34.39) * mm, "end": v(21.3, 34.35) * mm});
            skLineSegment(sketch, "E11.27.4", {"start": v(21.78, 34.3) * mm, "end": v(22.13, 34.08) * mm});
            skLineSegment(sketch, "E11.27.5", {"start": v(22.49, 33.85) * mm, "end": v(22.13, 34.08) * mm});
            skArc(sketch, "E11.27.6", {"start": v(22.72, 33.43) * mm, "mid": v(22.65, 33.67) * mm, "end": v(22.49, 33.85) * mm});
            skArc(sketch, "E11.27.7", {"start": v(22.48, 31.15) * mm, "mid": v(22.67, 32.28) * mm, "end": v(22.72, 33.43) * mm});
            skArc(sketch, "E11.27.8", {"start": v(22.21, 30.57) * mm, "mid": v(22.37, 30.85) * mm, "end": v(22.48, 31.15) * mm});
            skLineSegment(sketch, "E11.27.9", {"start": v(22.21, 30.57) * mm, "end": v(20.9, 28.77) * mm});
            skLineSegment(sketch, "E11.28.0", {"start": v(11.68, 35.94) * mm, "end": v(10.99, 33.82) * mm});
            skArc(sketch, "E11.28.1", {"start": v(12, 36.5) * mm, "mid": v(11.8, 36.23) * mm, "end": v(11.68, 35.94) * mm});
            skArc(sketch, "E11.28.2", {"start": v(12, 36.5) * mm, "mid": v(12.8, 37.31) * mm, "end": v(13.7, 38.03) * mm});
            skArc(sketch, "E11.28.3", {"start": v(14.17, 38.09) * mm, "mid": v(13.92, 38.12) * mm, "end": v(13.7, 38.03) * mm});
            skLineSegment(sketch, "E11.28.4", {"start": v(14.17, 38.09) * mm, "end": v(14.56, 37.94) * mm});
            skLineSegment(sketch, "E11.28.5", {"start": v(14.96, 37.78) * mm, "end": v(14.56, 37.94) * mm});
            skArc(sketch, "E11.28.6", {"start": v(15.27, 37.42) * mm, "mid": v(15.16, 37.64) * mm, "end": v(14.96, 37.78) * mm});
            skArc(sketch, "E11.28.7", {"start": v(15.5, 35.14) * mm, "mid": v(15.46, 36.3) * mm, "end": v(15.27, 37.42) * mm});
            skArc(sketch, "E11.28.8", {"start": v(15.37, 34.52) * mm, "mid": v(15.47, 34.83) * mm, "end": v(15.5, 35.14) * mm});
            skLineSegment(sketch, "E11.28.9", {"start": v(15.37, 34.52) * mm, "end": v(14.46, 32.49) * mm});
            skLineSegment(sketch, "E11.29.0", {"start": v(3.95, 37.58) * mm, "end": v(3.72, 35.37) * mm});
            skArc(sketch, "E11.29.1", {"start": v(4.14, 38.19) * mm, "mid": v(4.02, 37.9) * mm, "end": v(3.95, 37.58) * mm});
            skArc(sketch, "E11.29.2", {"start": v(4.14, 38.19) * mm, "mid": v(4.76, 39.16) * mm, "end": v(5.49, 40.04) * mm});
            skArc(sketch, "E11.29.3", {"start": v(5.94, 40.2) * mm, "mid": v(5.7, 40.18) * mm, "end": v(5.49, 40.04) * mm});
            skLineSegment(sketch, "E11.29.4", {"start": v(5.94, 40.2) * mm, "end": v(6.36, 40.13) * mm});
            skLineSegment(sketch, "E11.29.5", {"start": v(6.77, 40.07) * mm, "end": v(6.36, 40.13) * mm});
            skArc(sketch, "E11.29.6", {"start": v(7.16, 39.78) * mm, "mid": v(7, 39.97) * mm, "end": v(6.77, 40.07) * mm});
            skArc(sketch, "E11.29.7", {"start": v(7.86, 37.6) * mm, "mid": v(7.57, 38.71) * mm, "end": v(7.16, 39.78) * mm});
            skArc(sketch, "E11.29.8", {"start": v(7.86, 36.97) * mm, "mid": v(7.9, 37.28) * mm, "end": v(7.86, 37.6) * mm});
            skLineSegment(sketch, "E11.29.9", {"start": v(7.86, 36.97) * mm, "end": v(7.4, 34.78) * mm});
            skSolve(sketch);
        }
        {
            var Q0;
            {var subQ0=sQuery(id+"F0.wireOp",EDGE,"E0");var subQ33=makeQuery(id+"F0.imprint","INTERSECT",VERTEX,{"derivedFrom":[subQ0,sQuery(id+"F0.wireOp",EDGE,"E11.22.0")]});Q0=makeQuery(id+"F0.imprint","IMPRINT",FACE,{"disambiguationData":[TD([[makeQuery(id+"F0.imprint","IMPRINT",EDGE,{"disambiguationData":[TD([[subQ33,-1.0]])],"derivedFrom":subQ0}),1.0]])]});}
            cPlane(context, id + "F1", {"entities" : qUnion([Q0]), "cplaneType" : CPlaneType.OFFSET, "offset" : 22 * mm, "width" : 152.4 * mm, "height" : 152.4 * mm});
        }
        {
            var Q0;
            Q0=qCreatedBy(id+"F1.planeOp",FACE);
            var sketch = newSketch(context, id + "F2", { "sketchPlane" : qUnion([Q0])});
            skCircle(sketch, "E12", {"center": v(0, 0) * mm, "radius": 23.71 * mm});
            skArc(sketch, "E13.trimOffspring", {"start": v(-0.1, 25.66) * mm, "mid": v(-0.36, 26.25) * mm, "end": v(-0.66, 26.82) * mm});
            skLineSegment(sketch, "E14", {"start": v(0.01, 25.15) * mm, "end": v(0.09, 23.71) * mm});
            skLineSegment(sketch, "E15", {"start": v(-1.1, 27.08) * mm, "end": v(-1.42, 27.08) * mm});
            skLineSegment(sketch, "E16.MirrorCS", {"start": v(-1.74, 27.04) * mm, "end": v(-1.42, 27.08) * mm});
            skArc(sketch, "E17.MirrorCS", {"start": v(-2.58, 25.53) * mm, "mid": v(-2.39, 26.14) * mm, "end": v(-2.15, 26.74) * mm});
            skLineSegment(sketch, "E18.MirrorCS", {"start": v(-2.64, 25.01) * mm, "end": v(-2.57, 23.57) * mm});
            skPoint(sketch, "E19.visualSharp", {"position": v(-0.8, 27.08) * mm});
            skArc(sketch, "E19.filletArc", {"start": v(-0.66, 26.82) * mm, "mid": v(-0.84, 27) * mm, "end": v(-1.1, 27.08) * mm});
            skPoint(sketch, "E20.visualSharp", {"position": v(-2.03, 27.01) * mm});
            skArc(sketch, "E20.filletArc", {"start": v(-1.74, 27.04) * mm, "mid": v(-1.99, 26.95) * mm, "end": v(-2.15, 26.74) * mm});
            skPoint(sketch, "E21.visualSharp", {"position": v(0, 25.4) * mm});
            skArc(sketch, "E21.filletArc", {"start": v(0.01, 25.15) * mm, "mid": v(-0.02, 25.4) * mm, "end": v(-0.1, 25.66) * mm});
            skPoint(sketch, "E22.visualSharp", {"position": v(-2.66, 25.26) * mm});
            skArc(sketch, "E22.filletArc", {"start": v(-2.58, 25.53) * mm, "mid": v(-2.63, 25.27) * mm, "end": v(-2.64, 25.01) * mm});
            skSolve(sketch);
        }
        {
            var Q0;
            Q0=makeQuery(id+"F2.imprint","IMPRINT",FACE,{"disambiguationData":[TD([[makeQuery(id+"F2.imprint","IMPRINT",EDGE,{"derivedFrom":sQuery(id+"F2.wireOp",EDGE,"E13.trimOffspring")}),1.0]])]});
            var Q1;
            {var subQ0=sQuery(id+"F0.wireOp",EDGE,"E11.1.0");Q1=makeQuery(id+"F0.imprint","IMPRINT",FACE,{"disambiguationData":[TD([[makeQuery(id+"F0.imprint","IMPRINT",EDGE,{"derivedFrom":subQ0}),1.0]])]});}
            loft(context, id + "F3", {"sheetProfilesArray" : [{ "sheetProfileEntities" : qUnion([Q0]) }, { "sheetProfileEntities" : qUnion([Q1]) }]});
        }
        {
            var Q0;
            Q0=qCreatedBy(id+"F1.planeOp",FACE);
            var sketch = newSketch(context, id + "F4", { "sketchPlane" : qUnion([Q0])});
            skCircle(sketch, "E23", {"center": v(0, 0) * mm, "radius": 23.71 * mm});
            skSolve(sketch);
        }
        {
            var Q0;
            Q0=qCreatedBy(makeId("Front.planeOp"),FACE);
            var sketch = newSketch(context, id + "F5", { "sketchPlane" : qUnion([Q0])});
            skCircle(sketch, "E24", {"center": v(0, 0) * mm, "radius": 35.56 * mm});
            skSolve(sketch);
        }
        {
            var Q1;
            Q1=makeQuery(id+"F4.imprint","IMPRINT",FACE,{"disambiguationData":[TD([[makeQuery(id+"F4.imprint","IMPRINT",EDGE,{"derivedFrom":sQuery(id+"F4.wireOp",EDGE,"E23")}),1.0]])]});
            var Q2;
            Q2=makeQuery(id+"F5.imprint","IMPRINT",FACE,{"disambiguationData":[TD([[makeQuery(id+"F5.imprint","IMPRINT",EDGE,{"derivedFrom":sQuery(id+"F5.wireOp",EDGE,"E24")}),1.0]])]});
            loft(context, id + "F6", {"operationType" : NewBodyOperationType.ADD, "sheetProfilesArray" : [{ "sheetProfileEntities" : qUnion([Q1]) }, { "sheetProfileEntities" : qUnion([Q2]) }]});
        }
        {
            var Q0;
            {var subQ3=sQuery(id+"F0.wireOp",EDGE,"E11.1.0");Q0=makeQuery(id+"F3.opLoft","SWEPT_BODY",BODY,{"disambiguationData":[OSD([makeQuery(id+"F0.imprint","IMPRINT",FACE,{"disambiguationData":[TD([[makeQuery(id+"F0.imprint","IMPRINT",EDGE,{"derivedFrom":subQ3}),1.0]])]}),makeQuery(id+"F2.imprint","IMPRINT",FACE,{"disambiguationData":[TD([[makeQuery(id+"F2.imprint","IMPRINT",EDGE,{"derivedFrom":sQuery(id+"F2.wireOp",EDGE,"E13.trimOffspring")}),1.0]])]})])]});}
            var Q1;
            Q1=makeQuery(id+"F6.opLoft","SWEPT_FACE",FACE,{"disambiguationData":[OSD([sQuery(id+"F4.wireOp",EDGE,"E23"),sQuery(id+"F5.wireOp",EDGE,"E24")])]});
            circularPattern(context, id + "F7", {"entities" : qUnion([Q0]), "axis" : qUnion([Q1]), "angle" : 360 * degree, "instanceCount" : 30, "equalSpace" : true});
        }
        {
            var Q0;
            {var subQ3=sQuery(id+"F0.wireOp",EDGE,"E11.1.0");Q0=makeQuery(id+"F3.opLoft","SWEPT_BODY",BODY,{"disambiguationData":[OSD([makeQuery(id+"F0.imprint","IMPRINT",FACE,{"disambiguationData":[TD([[makeQuery(id+"F0.imprint","IMPRINT",EDGE,{"derivedFrom":subQ3}),1.0]])]}),makeQuery(id+"F2.imprint","IMPRINT",FACE,{"disambiguationData":[TD([[makeQuery(id+"F2.imprint","IMPRINT",EDGE,{"derivedFrom":sQuery(id+"F2.wireOp",EDGE,"E13.trimOffspring")}),1.0]])]})])]});}
            var Q1;
            {var subQ3=sQuery(id+"F0.wireOp",EDGE,"E11.1.0");Q1=makeQuery(id+"F7.opPattern","COPY",BODY,{"derivedFrom":makeQuery(id+"F3.opLoft","SWEPT_BODY",BODY,{"disambiguationData":[OSD([makeQuery(id+"F0.imprint","IMPRINT",FACE,{"disambiguationData":[TD([[makeQuery(id+"F0.imprint","IMPRINT",EDGE,{"derivedFrom":subQ3}),1.0]])]}),makeQuery(id+"F2.imprint","IMPRINT",FACE,{"disambiguationData":[TD([[makeQuery(id+"F2.imprint","IMPRINT",EDGE,{"derivedFrom":sQuery(id+"F2.wireOp",EDGE,"E13.trimOffspring")}),1.0]])]})])]}),"instanceName":"29"});}
            var Q2;
            {var subQ3=sQuery(id+"F0.wireOp",EDGE,"E11.1.0");Q2=makeQuery(id+"F7.opPattern","COPY",BODY,{"derivedFrom":makeQuery(id+"F3.opLoft","SWEPT_BODY",BODY,{"disambiguationData":[OSD([makeQuery(id+"F0.imprint","IMPRINT",FACE,{"disambiguationData":[TD([[makeQuery(id+"F0.imprint","IMPRINT",EDGE,{"derivedFrom":subQ3}),1.0]])]}),makeQuery(id+"F2.imprint","IMPRINT",FACE,{"disambiguationData":[TD([[makeQuery(id+"F2.imprint","IMPRINT",EDGE,{"derivedFrom":sQuery(id+"F2.wireOp",EDGE,"E13.trimOffspring")}),1.0]])]})])]}),"instanceName":"28"});}
            var Q3;
            {var subQ3=sQuery(id+"F0.wireOp",EDGE,"E11.1.0");Q3=makeQuery(id+"F7.opPattern","COPY",BODY,{"derivedFrom":makeQuery(id+"F3.opLoft","SWEPT_BODY",BODY,{"disambiguationData":[OSD([makeQuery(id+"F0.imprint","IMPRINT",FACE,{"disambiguationData":[TD([[makeQuery(id+"F0.imprint","IMPRINT",EDGE,{"derivedFrom":subQ3}),1.0]])]}),makeQuery(id+"F2.imprint","IMPRINT",FACE,{"disambiguationData":[TD([[makeQuery(id+"F2.imprint","IMPRINT",EDGE,{"derivedFrom":sQuery(id+"F2.wireOp",EDGE,"E13.trimOffspring")}),1.0]])]})])]}),"instanceName":"1"});}
            var Q4;
            {var subQ3=sQuery(id+"F0.wireOp",EDGE,"E11.1.0");Q4=makeQuery(id+"F7.opPattern","COPY",BODY,{"derivedFrom":makeQuery(id+"F3.opLoft","SWEPT_BODY",BODY,{"disambiguationData":[OSD([makeQuery(id+"F0.imprint","IMPRINT",FACE,{"disambiguationData":[TD([[makeQuery(id+"F0.imprint","IMPRINT",EDGE,{"derivedFrom":subQ3}),1.0]])]}),makeQuery(id+"F2.imprint","IMPRINT",FACE,{"disambiguationData":[TD([[makeQuery(id+"F2.imprint","IMPRINT",EDGE,{"derivedFrom":sQuery(id+"F2.wireOp",EDGE,"E13.trimOffspring")}),1.0]])]})])]}),"instanceName":"2"});}
            var Q5;
            {var subQ3=sQuery(id+"F0.wireOp",EDGE,"E11.1.0");Q5=makeQuery(id+"F7.opPattern","COPY",BODY,{"derivedFrom":makeQuery(id+"F3.opLoft","SWEPT_BODY",BODY,{"disambiguationData":[OSD([makeQuery(id+"F0.imprint","IMPRINT",FACE,{"disambiguationData":[TD([[makeQuery(id+"F0.imprint","IMPRINT",EDGE,{"derivedFrom":subQ3}),1.0]])]}),makeQuery(id+"F2.imprint","IMPRINT",FACE,{"disambiguationData":[TD([[makeQuery(id+"F2.imprint","IMPRINT",EDGE,{"derivedFrom":sQuery(id+"F2.wireOp",EDGE,"E13.trimOffspring")}),1.0]])]})])]}),"instanceName":"3"});}
            var Q6;
            {var subQ3=sQuery(id+"F0.wireOp",EDGE,"E11.1.0");Q6=makeQuery(id+"F7.opPattern","COPY",BODY,{"derivedFrom":makeQuery(id+"F3.opLoft","SWEPT_BODY",BODY,{"disambiguationData":[OSD([makeQuery(id+"F0.imprint","IMPRINT",FACE,{"disambiguationData":[TD([[makeQuery(id+"F0.imprint","IMPRINT",EDGE,{"derivedFrom":subQ3}),1.0]])]}),makeQuery(id+"F2.imprint","IMPRINT",FACE,{"disambiguationData":[TD([[makeQuery(id+"F2.imprint","IMPRINT",EDGE,{"derivedFrom":sQuery(id+"F2.wireOp",EDGE,"E13.trimOffspring")}),1.0]])]})])]}),"instanceName":"4"});}
            var Q7;
            {var subQ3=sQuery(id+"F0.wireOp",EDGE,"E11.1.0");Q7=makeQuery(id+"F7.opPattern","COPY",BODY,{"derivedFrom":makeQuery(id+"F3.opLoft","SWEPT_BODY",BODY,{"disambiguationData":[OSD([makeQuery(id+"F0.imprint","IMPRINT",FACE,{"disambiguationData":[TD([[makeQuery(id+"F0.imprint","IMPRINT",EDGE,{"derivedFrom":subQ3}),1.0]])]}),makeQuery(id+"F2.imprint","IMPRINT",FACE,{"disambiguationData":[TD([[makeQuery(id+"F2.imprint","IMPRINT",EDGE,{"derivedFrom":sQuery(id+"F2.wireOp",EDGE,"E13.trimOffspring")}),1.0]])]})])]}),"instanceName":"5"});}
            var Q8;
            {var subQ3=sQuery(id+"F0.wireOp",EDGE,"E11.1.0");Q8=makeQuery(id+"F7.opPattern","COPY",BODY,{"derivedFrom":makeQuery(id+"F3.opLoft","SWEPT_BODY",BODY,{"disambiguationData":[OSD([makeQuery(id+"F0.imprint","IMPRINT",FACE,{"disambiguationData":[TD([[makeQuery(id+"F0.imprint","IMPRINT",EDGE,{"derivedFrom":subQ3}),1.0]])]}),makeQuery(id+"F2.imprint","IMPRINT",FACE,{"disambiguationData":[TD([[makeQuery(id+"F2.imprint","IMPRINT",EDGE,{"derivedFrom":sQuery(id+"F2.wireOp",EDGE,"E13.trimOffspring")}),1.0]])]})])]}),"instanceName":"6"});}
            var Q9;
            {var subQ3=sQuery(id+"F0.wireOp",EDGE,"E11.1.0");Q9=makeQuery(id+"F7.opPattern","COPY",BODY,{"derivedFrom":makeQuery(id+"F3.opLoft","SWEPT_BODY",BODY,{"disambiguationData":[OSD([makeQuery(id+"F0.imprint","IMPRINT",FACE,{"disambiguationData":[TD([[makeQuery(id+"F0.imprint","IMPRINT",EDGE,{"derivedFrom":subQ3}),1.0]])]}),makeQuery(id+"F2.imprint","IMPRINT",FACE,{"disambiguationData":[TD([[makeQuery(id+"F2.imprint","IMPRINT",EDGE,{"derivedFrom":sQuery(id+"F2.wireOp",EDGE,"E13.trimOffspring")}),1.0]])]})])]}),"instanceName":"7"});}
            var Q10;
            {var subQ3=sQuery(id+"F0.wireOp",EDGE,"E11.1.0");Q10=makeQuery(id+"F7.opPattern","COPY",BODY,{"derivedFrom":makeQuery(id+"F3.opLoft","SWEPT_BODY",BODY,{"disambiguationData":[OSD([makeQuery(id+"F0.imprint","IMPRINT",FACE,{"disambiguationData":[TD([[makeQuery(id+"F0.imprint","IMPRINT",EDGE,{"derivedFrom":subQ3}),1.0]])]}),makeQuery(id+"F2.imprint","IMPRINT",FACE,{"disambiguationData":[TD([[makeQuery(id+"F2.imprint","IMPRINT",EDGE,{"derivedFrom":sQuery(id+"F2.wireOp",EDGE,"E13.trimOffspring")}),1.0]])]})])]}),"instanceName":"8"});}
            var Q11;
            {var subQ3=sQuery(id+"F0.wireOp",EDGE,"E11.1.0");Q11=makeQuery(id+"F7.opPattern","COPY",BODY,{"derivedFrom":makeQuery(id+"F3.opLoft","SWEPT_BODY",BODY,{"disambiguationData":[OSD([makeQuery(id+"F0.imprint","IMPRINT",FACE,{"disambiguationData":[TD([[makeQuery(id+"F0.imprint","IMPRINT",EDGE,{"derivedFrom":subQ3}),1.0]])]}),makeQuery(id+"F2.imprint","IMPRINT",FACE,{"disambiguationData":[TD([[makeQuery(id+"F2.imprint","IMPRINT",EDGE,{"derivedFrom":sQuery(id+"F2.wireOp",EDGE,"E13.trimOffspring")}),1.0]])]})])]}),"instanceName":"9"});}
            var Q12;
            {var subQ3=sQuery(id+"F0.wireOp",EDGE,"E11.1.0");Q12=makeQuery(id+"F7.opPattern","COPY",BODY,{"derivedFrom":makeQuery(id+"F3.opLoft","SWEPT_BODY",BODY,{"disambiguationData":[OSD([makeQuery(id+"F0.imprint","IMPRINT",FACE,{"disambiguationData":[TD([[makeQuery(id+"F0.imprint","IMPRINT",EDGE,{"derivedFrom":subQ3}),1.0]])]}),makeQuery(id+"F2.imprint","IMPRINT",FACE,{"disambiguationData":[TD([[makeQuery(id+"F2.imprint","IMPRINT",EDGE,{"derivedFrom":sQuery(id+"F2.wireOp",EDGE,"E13.trimOffspring")}),1.0]])]})])]}),"instanceName":"11"});}
            var Q13;
            {var subQ3=sQuery(id+"F0.wireOp",EDGE,"E11.1.0");Q13=makeQuery(id+"F7.opPattern","COPY",BODY,{"derivedFrom":makeQuery(id+"F3.opLoft","SWEPT_BODY",BODY,{"disambiguationData":[OSD([makeQuery(id+"F0.imprint","IMPRINT",FACE,{"disambiguationData":[TD([[makeQuery(id+"F0.imprint","IMPRINT",EDGE,{"derivedFrom":subQ3}),1.0]])]}),makeQuery(id+"F2.imprint","IMPRINT",FACE,{"disambiguationData":[TD([[makeQuery(id+"F2.imprint","IMPRINT",EDGE,{"derivedFrom":sQuery(id+"F2.wireOp",EDGE,"E13.trimOffspring")}),1.0]])]})])]}),"instanceName":"12"});}
            var Q14;
            {var subQ3=sQuery(id+"F0.wireOp",EDGE,"E11.1.0");Q14=makeQuery(id+"F7.opPattern","COPY",BODY,{"derivedFrom":makeQuery(id+"F3.opLoft","SWEPT_BODY",BODY,{"disambiguationData":[OSD([makeQuery(id+"F0.imprint","IMPRINT",FACE,{"disambiguationData":[TD([[makeQuery(id+"F0.imprint","IMPRINT",EDGE,{"derivedFrom":subQ3}),1.0]])]}),makeQuery(id+"F2.imprint","IMPRINT",FACE,{"disambiguationData":[TD([[makeQuery(id+"F2.imprint","IMPRINT",EDGE,{"derivedFrom":sQuery(id+"F2.wireOp",EDGE,"E13.trimOffspring")}),1.0]])]})])]}),"instanceName":"13"});}
            var Q15;
            {var subQ3=sQuery(id+"F0.wireOp",EDGE,"E11.1.0");Q15=makeQuery(id+"F7.opPattern","COPY",BODY,{"derivedFrom":makeQuery(id+"F3.opLoft","SWEPT_BODY",BODY,{"disambiguationData":[OSD([makeQuery(id+"F0.imprint","IMPRINT",FACE,{"disambiguationData":[TD([[makeQuery(id+"F0.imprint","IMPRINT",EDGE,{"derivedFrom":subQ3}),1.0]])]}),makeQuery(id+"F2.imprint","IMPRINT",FACE,{"disambiguationData":[TD([[makeQuery(id+"F2.imprint","IMPRINT",EDGE,{"derivedFrom":sQuery(id+"F2.wireOp",EDGE,"E13.trimOffspring")}),1.0]])]})])]}),"instanceName":"14"});}
            var Q16;
            {var subQ3=sQuery(id+"F0.wireOp",EDGE,"E11.1.0");Q16=makeQuery(id+"F7.opPattern","COPY",BODY,{"derivedFrom":makeQuery(id+"F3.opLoft","SWEPT_BODY",BODY,{"disambiguationData":[OSD([makeQuery(id+"F0.imprint","IMPRINT",FACE,{"disambiguationData":[TD([[makeQuery(id+"F0.imprint","IMPRINT",EDGE,{"derivedFrom":subQ3}),1.0]])]}),makeQuery(id+"F2.imprint","IMPRINT",FACE,{"disambiguationData":[TD([[makeQuery(id+"F2.imprint","IMPRINT",EDGE,{"derivedFrom":sQuery(id+"F2.wireOp",EDGE,"E13.trimOffspring")}),1.0]])]})])]}),"instanceName":"15"});}
            var Q17;
            {var subQ3=sQuery(id+"F0.wireOp",EDGE,"E11.1.0");Q17=makeQuery(id+"F7.opPattern","COPY",BODY,{"derivedFrom":makeQuery(id+"F3.opLoft","SWEPT_BODY",BODY,{"disambiguationData":[OSD([makeQuery(id+"F0.imprint","IMPRINT",FACE,{"disambiguationData":[TD([[makeQuery(id+"F0.imprint","IMPRINT",EDGE,{"derivedFrom":subQ3}),1.0]])]}),makeQuery(id+"F2.imprint","IMPRINT",FACE,{"disambiguationData":[TD([[makeQuery(id+"F2.imprint","IMPRINT",EDGE,{"derivedFrom":sQuery(id+"F2.wireOp",EDGE,"E13.trimOffspring")}),1.0]])]})])]}),"instanceName":"16"});}
            var Q18;
            {var subQ3=sQuery(id+"F0.wireOp",EDGE,"E11.1.0");Q18=makeQuery(id+"F7.opPattern","COPY",BODY,{"derivedFrom":makeQuery(id+"F3.opLoft","SWEPT_BODY",BODY,{"disambiguationData":[OSD([makeQuery(id+"F0.imprint","IMPRINT",FACE,{"disambiguationData":[TD([[makeQuery(id+"F0.imprint","IMPRINT",EDGE,{"derivedFrom":subQ3}),1.0]])]}),makeQuery(id+"F2.imprint","IMPRINT",FACE,{"disambiguationData":[TD([[makeQuery(id+"F2.imprint","IMPRINT",EDGE,{"derivedFrom":sQuery(id+"F2.wireOp",EDGE,"E13.trimOffspring")}),1.0]])]})])]}),"instanceName":"17"});}
            var Q19;
            {var subQ3=sQuery(id+"F0.wireOp",EDGE,"E11.1.0");Q19=makeQuery(id+"F7.opPattern","COPY",BODY,{"derivedFrom":makeQuery(id+"F3.opLoft","SWEPT_BODY",BODY,{"disambiguationData":[OSD([makeQuery(id+"F0.imprint","IMPRINT",FACE,{"disambiguationData":[TD([[makeQuery(id+"F0.imprint","IMPRINT",EDGE,{"derivedFrom":subQ3}),1.0]])]}),makeQuery(id+"F2.imprint","IMPRINT",FACE,{"disambiguationData":[TD([[makeQuery(id+"F2.imprint","IMPRINT",EDGE,{"derivedFrom":sQuery(id+"F2.wireOp",EDGE,"E13.trimOffspring")}),1.0]])]})])]}),"instanceName":"18"});}
            var Q20;
            {var subQ3=sQuery(id+"F0.wireOp",EDGE,"E11.1.0");Q20=makeQuery(id+"F7.opPattern","COPY",BODY,{"derivedFrom":makeQuery(id+"F3.opLoft","SWEPT_BODY",BODY,{"disambiguationData":[OSD([makeQuery(id+"F0.imprint","IMPRINT",FACE,{"disambiguationData":[TD([[makeQuery(id+"F0.imprint","IMPRINT",EDGE,{"derivedFrom":subQ3}),1.0]])]}),makeQuery(id+"F2.imprint","IMPRINT",FACE,{"disambiguationData":[TD([[makeQuery(id+"F2.imprint","IMPRINT",EDGE,{"derivedFrom":sQuery(id+"F2.wireOp",EDGE,"E13.trimOffspring")}),1.0]])]})])]}),"instanceName":"19"});}
            var Q21;
            {var subQ3=sQuery(id+"F0.wireOp",EDGE,"E11.1.0");Q21=makeQuery(id+"F7.opPattern","COPY",BODY,{"derivedFrom":makeQuery(id+"F3.opLoft","SWEPT_BODY",BODY,{"disambiguationData":[OSD([makeQuery(id+"F0.imprint","IMPRINT",FACE,{"disambiguationData":[TD([[makeQuery(id+"F0.imprint","IMPRINT",EDGE,{"derivedFrom":subQ3}),1.0]])]}),makeQuery(id+"F2.imprint","IMPRINT",FACE,{"disambiguationData":[TD([[makeQuery(id+"F2.imprint","IMPRINT",EDGE,{"derivedFrom":sQuery(id+"F2.wireOp",EDGE,"E13.trimOffspring")}),1.0]])]})])]}),"instanceName":"20"});}
            var Q22;
            {var subQ3=sQuery(id+"F0.wireOp",EDGE,"E11.1.0");Q22=makeQuery(id+"F7.opPattern","COPY",BODY,{"derivedFrom":makeQuery(id+"F3.opLoft","SWEPT_BODY",BODY,{"disambiguationData":[OSD([makeQuery(id+"F0.imprint","IMPRINT",FACE,{"disambiguationData":[TD([[makeQuery(id+"F0.imprint","IMPRINT",EDGE,{"derivedFrom":subQ3}),1.0]])]}),makeQuery(id+"F2.imprint","IMPRINT",FACE,{"disambiguationData":[TD([[makeQuery(id+"F2.imprint","IMPRINT",EDGE,{"derivedFrom":sQuery(id+"F2.wireOp",EDGE,"E13.trimOffspring")}),1.0]])]})])]}),"instanceName":"21"});}
            var Q23;
            {var subQ3=sQuery(id+"F0.wireOp",EDGE,"E11.1.0");Q23=makeQuery(id+"F7.opPattern","COPY",BODY,{"derivedFrom":makeQuery(id+"F3.opLoft","SWEPT_BODY",BODY,{"disambiguationData":[OSD([makeQuery(id+"F0.imprint","IMPRINT",FACE,{"disambiguationData":[TD([[makeQuery(id+"F0.imprint","IMPRINT",EDGE,{"derivedFrom":subQ3}),1.0]])]}),makeQuery(id+"F2.imprint","IMPRINT",FACE,{"disambiguationData":[TD([[makeQuery(id+"F2.imprint","IMPRINT",EDGE,{"derivedFrom":sQuery(id+"F2.wireOp",EDGE,"E13.trimOffspring")}),1.0]])]})])]}),"instanceName":"22"});}
            var Q24;
            {var subQ3=sQuery(id+"F0.wireOp",EDGE,"E11.1.0");Q24=makeQuery(id+"F7.opPattern","COPY",BODY,{"derivedFrom":makeQuery(id+"F3.opLoft","SWEPT_BODY",BODY,{"disambiguationData":[OSD([makeQuery(id+"F0.imprint","IMPRINT",FACE,{"disambiguationData":[TD([[makeQuery(id+"F0.imprint","IMPRINT",EDGE,{"derivedFrom":subQ3}),1.0]])]}),makeQuery(id+"F2.imprint","IMPRINT",FACE,{"disambiguationData":[TD([[makeQuery(id+"F2.imprint","IMPRINT",EDGE,{"derivedFrom":sQuery(id+"F2.wireOp",EDGE,"E13.trimOffspring")}),1.0]])]})])]}),"instanceName":"23"});}
            var Q25;
            {var subQ3=sQuery(id+"F0.wireOp",EDGE,"E11.1.0");Q25=makeQuery(id+"F7.opPattern","COPY",BODY,{"derivedFrom":makeQuery(id+"F3.opLoft","SWEPT_BODY",BODY,{"disambiguationData":[OSD([makeQuery(id+"F0.imprint","IMPRINT",FACE,{"disambiguationData":[TD([[makeQuery(id+"F0.imprint","IMPRINT",EDGE,{"derivedFrom":subQ3}),1.0]])]}),makeQuery(id+"F2.imprint","IMPRINT",FACE,{"disambiguationData":[TD([[makeQuery(id+"F2.imprint","IMPRINT",EDGE,{"derivedFrom":sQuery(id+"F2.wireOp",EDGE,"E13.trimOffspring")}),1.0]])]})])]}),"instanceName":"24"});}
            var Q26;
            {var subQ3=sQuery(id+"F0.wireOp",EDGE,"E11.1.0");Q26=makeQuery(id+"F7.opPattern","COPY",BODY,{"derivedFrom":makeQuery(id+"F3.opLoft","SWEPT_BODY",BODY,{"disambiguationData":[OSD([makeQuery(id+"F0.imprint","IMPRINT",FACE,{"disambiguationData":[TD([[makeQuery(id+"F0.imprint","IMPRINT",EDGE,{"derivedFrom":subQ3}),1.0]])]}),makeQuery(id+"F2.imprint","IMPRINT",FACE,{"disambiguationData":[TD([[makeQuery(id+"F2.imprint","IMPRINT",EDGE,{"derivedFrom":sQuery(id+"F2.wireOp",EDGE,"E13.trimOffspring")}),1.0]])]})])]}),"instanceName":"25"});}
            var Q27;
            {var subQ3=sQuery(id+"F0.wireOp",EDGE,"E11.1.0");Q27=makeQuery(id+"F7.opPattern","COPY",BODY,{"derivedFrom":makeQuery(id+"F3.opLoft","SWEPT_BODY",BODY,{"disambiguationData":[OSD([makeQuery(id+"F0.imprint","IMPRINT",FACE,{"disambiguationData":[TD([[makeQuery(id+"F0.imprint","IMPRINT",EDGE,{"derivedFrom":subQ3}),1.0]])]}),makeQuery(id+"F2.imprint","IMPRINT",FACE,{"disambiguationData":[TD([[makeQuery(id+"F2.imprint","IMPRINT",EDGE,{"derivedFrom":sQuery(id+"F2.wireOp",EDGE,"E13.trimOffspring")}),1.0]])]})])]}),"instanceName":"26"});}
            var Q28;
            {var subQ3=sQuery(id+"F0.wireOp",EDGE,"E11.1.0");Q28=makeQuery(id+"F7.opPattern","COPY",BODY,{"derivedFrom":makeQuery(id+"F3.opLoft","SWEPT_BODY",BODY,{"disambiguationData":[OSD([makeQuery(id+"F0.imprint","IMPRINT",FACE,{"disambiguationData":[TD([[makeQuery(id+"F0.imprint","IMPRINT",EDGE,{"derivedFrom":subQ3}),1.0]])]}),makeQuery(id+"F2.imprint","IMPRINT",FACE,{"disambiguationData":[TD([[makeQuery(id+"F2.imprint","IMPRINT",EDGE,{"derivedFrom":sQuery(id+"F2.wireOp",EDGE,"E13.trimOffspring")}),1.0]])]})])]}),"instanceName":"27"});}
            var Q29;
            {var subQ3=sQuery(id+"F0.wireOp",EDGE,"E11.1.0");Q29=makeQuery(id+"F7.opPattern","COPY",BODY,{"derivedFrom":makeQuery(id+"F3.opLoft","SWEPT_BODY",BODY,{"disambiguationData":[OSD([makeQuery(id+"F0.imprint","IMPRINT",FACE,{"disambiguationData":[TD([[makeQuery(id+"F0.imprint","IMPRINT",EDGE,{"derivedFrom":subQ3}),1.0]])]}),makeQuery(id+"F2.imprint","IMPRINT",FACE,{"disambiguationData":[TD([[makeQuery(id+"F2.imprint","IMPRINT",EDGE,{"derivedFrom":sQuery(id+"F2.wireOp",EDGE,"E13.trimOffspring")}),1.0]])]})])]}),"instanceName":"10"});}
            booleanBodies(context, id + "F8", {"operationType" : BooleanOperationType.UNION, "tools" : qUnion([Q0, Q1, Q2, Q3, Q4, Q5, Q6, Q7, Q8, Q9, Q10, Q11, Q12, Q13, Q14, Q15, Q16, Q17, Q18, Q19, Q20, Q21, Q22, Q23, Q24, Q25, Q26, Q27, Q28, Q29])});
        }
        {
            var Q0;
            {var subQ3=makeQuery(id+"F6.boolean.opBoolean","MERGE",FACE,{"derivedFrom":[makeQuery(id+"F3.opLoft","CAP_FACE",FACE,{"disambiguationData":[OSD([makeQuery(id+"F2.imprint","IMPRINT",FACE,{"disambiguationData":[TD([[makeQuery(id+"F2.imprint","IMPRINT",EDGE,{"derivedFrom":sQuery(id+"F2.wireOp",EDGE,"E13.trimOffspring")}),1.0]])]})])],"isStart":true}),makeQuery(id+"F6.opLoft","CAP_FACE",FACE,{"disambiguationData":[OSD([makeQuery(id+"F4.imprint","IMPRINT",FACE,{"disambiguationData":[TD([[makeQuery(id+"F4.imprint","IMPRINT",EDGE,{"derivedFrom":sQuery(id+"F4.wireOp",EDGE,"E23")}),1.0]])]})])],"isStart":true})]});Q0=makeQuery(id+"F8.opBoolean","MERGE",FACE,{"derivedFrom":[subQ3,makeQuery(id+"F7.opPattern","COPY",FACE,{"derivedFrom":subQ3,"instanceName":"1"}),makeQuery(id+"F7.opPattern","COPY",FACE,{"derivedFrom":subQ3,"instanceName":"2"}),makeQuery(id+"F7.opPattern","COPY",FACE,{"derivedFrom":subQ3,"instanceName":"3"}),makeQuery(id+"F7.opPattern","COPY",FACE,{"derivedFrom":subQ3,"instanceName":"4"}),makeQuery(id+"F7.opPattern","COPY",FACE,{"derivedFrom":subQ3,"instanceName":"5"}),makeQuery(id+"F7.opPattern","COPY",FACE,{"derivedFrom":subQ3,"instanceName":"6"}),makeQuery(id+"F7.opPattern","COPY",FACE,{"derivedFrom":subQ3,"instanceName":"7"}),makeQuery(id+"F7.opPattern","COPY",FACE,{"derivedFrom":subQ3,"instanceName":"8"}),makeQuery(id+"F7.opPattern","COPY",FACE,{"derivedFrom":subQ3,"instanceName":"9"}),makeQuery(id+"F7.opPattern","COPY",FACE,{"derivedFrom":subQ3,"instanceName":"10"}),makeQuery(id+"F7.opPattern","COPY",FACE,{"derivedFrom":subQ3,"instanceName":"11"}),makeQuery(id+"F7.opPattern","COPY",FACE,{"derivedFrom":subQ3,"instanceName":"12"}),makeQuery(id+"F7.opPattern","COPY",FACE,{"derivedFrom":subQ3,"instanceName":"13"}),makeQuery(id+"F7.opPattern","COPY",FACE,{"derivedFrom":subQ3,"instanceName":"14"}),makeQuery(id+"F7.opPattern","COPY",FACE,{"derivedFrom":subQ3,"instanceName":"15"}),makeQuery(id+"F7.opPattern","COPY",FACE,{"derivedFrom":subQ3,"instanceName":"16"}),makeQuery(id+"F7.opPattern","COPY",FACE,{"derivedFrom":subQ3,"instanceName":"17"}),makeQuery(id+"F7.opPattern","COPY",FACE,{"derivedFrom":subQ3,"instanceName":"18"}),makeQuery(id+"F7.opPattern","COPY",FACE,{"derivedFrom":subQ3,"instanceName":"19"}),makeQuery(id+"F7.opPattern","COPY",FACE,{"derivedFrom":subQ3,"instanceName":"20"}),makeQuery(id+"F7.opPattern","COPY",FACE,{"derivedFrom":subQ3,"instanceName":"21"}),makeQuery(id+"F7.opPattern","COPY",FACE,{"derivedFrom":subQ3,"instanceName":"22"}),makeQuery(id+"F7.opPattern","COPY",FACE,{"derivedFrom":subQ3,"instanceName":"23"}),makeQuery(id+"F7.opPattern","COPY",FACE,{"derivedFrom":subQ3,"instanceName":"24"}),makeQuery(id+"F7.opPattern","COPY",FACE,{"derivedFrom":subQ3,"instanceName":"25"}),makeQuery(id+"F7.opPattern","COPY",FACE,{"derivedFrom":subQ3,"instanceName":"26"}),makeQuery(id+"F7.opPattern","COPY",FACE,{"derivedFrom":subQ3,"instanceName":"27"}),makeQuery(id+"F7.opPattern","COPY",FACE,{"derivedFrom":subQ3,"instanceName":"28"}),makeQuery(id+"F7.opPattern","COPY",FACE,{"derivedFrom":subQ3,"instanceName":"29"})]});}
            var sketch = newSketch(context, id + "F9", { "sketchPlane" : qUnion([Q0])});
            skPoint(sketch, "E25", {"position": v(0, 0) * mm});
            skSolve(sketch);
        }
        {
            var Q0;
            Q0=sQuery(id+"F9.wireOp",VERTEX,"E25");
            var Q1;
            {var subQ3=sQuery(id+"F0.wireOp",EDGE,"E11.1.0");Q1=makeQuery(id+"F3.opLoft","SWEPT_BODY",BODY,{"disambiguationData":[OSD([makeQuery(id+"F0.imprint","IMPRINT",FACE,{"disambiguationData":[TD([[makeQuery(id+"F0.imprint","IMPRINT",EDGE,{"derivedFrom":subQ3}),1.0]])]}),makeQuery(id+"F2.imprint","IMPRINT",FACE,{"disambiguationData":[TD([[makeQuery(id+"F2.imprint","IMPRINT",EDGE,{"derivedFrom":sQuery(id+"F2.wireOp",EDGE,"E13.trimOffspring")}),1.0]])]})])]});}
            hole(context, id + "F10", {"style" : HoleStyle.SIMPLE, "endStyle" : HoleEndStyle.THROUGH, "holeDiameter" : 12.7 * mm, "tappedDepth" : 12.7 * mm, "tapClearance" : 3, "locations" : qUnion([Q0]), "scope" : qUnion([Q1])});
        }
    });
